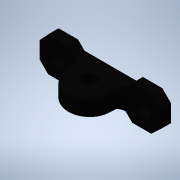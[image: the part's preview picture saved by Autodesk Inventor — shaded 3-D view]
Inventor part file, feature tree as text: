
AUTODESK INVENTOR PART (.ipt)
format: ipt  version: 2020 (Build 240168000, 168)  size: 387,072 bytes
history: native  units: in
note: dims shown in document units (in); Inventor stores cm internally (conversion verified against a paired STEP export)
features: other x4, plane x1, imported_body x1
ambient origin geometry x8: Origin, YZ Plane, XZ Plane, XY Plane, X Axis, Y Axis, Z Axis, Center Point
bodies: Body1 (feature_tree)
feature tree (6):
  other  "Pillow Block"
  parser-record x1  (decoder bookkeeping rows leaked as tree rows — omitted from the tree; the rows remain in map.json)
  plane  "Work Plane1"
  imported_body  "Base1"
  other  "Work Axis4"
  other  "Work Axis5"
